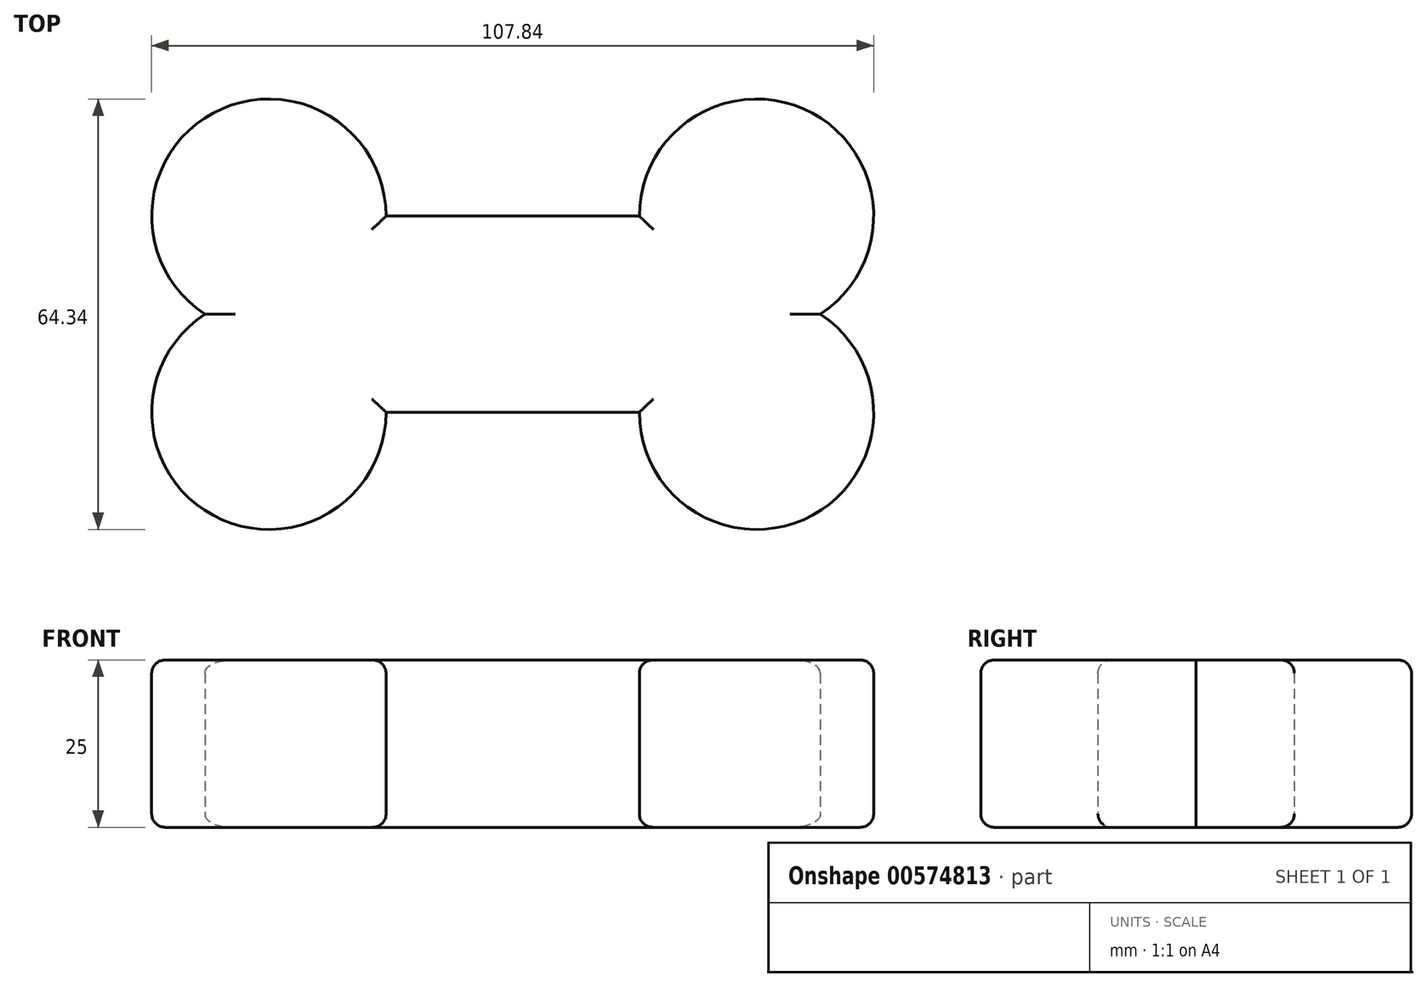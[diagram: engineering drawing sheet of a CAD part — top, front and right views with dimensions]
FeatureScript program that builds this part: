
annotation { "Feature Type Name" : "Feature", "Feature Type Description" : "" }
export const myFeature = defineFeature(function(context is Context, id is Id, definition is map)
    precondition{}
    {
        {
            var Q0;
            Q0=qCreatedBy(makeId("Top.planeOp"),FACE);
            var sketch = newSketch(context, id + "F0", { "sketchPlane" : qUnion([Q0])});
            skLineSegment(sketch, "E0.bottom", {"start": v(36.42, 14.67) * mm, "end": v(-36.42, 14.67) * mm});
            skLineSegment(sketch, "E0.top", {"start": v(36.42, -14.67) * mm, "end": v(-36.42, -14.67) * mm});
            skLineSegment(sketch, "E0.left", {"start": v(36.42, 14.67) * mm, "end": v(36.42, -14.67) * mm});
            skLineSegment(sketch, "E0.right", {"start": v(-36.42, 14.67) * mm, "end": v(-36.42, -14.67) * mm});
            skPoint(sketch, "E0.middle", {"position": v(0, 0) * mm});
            skCircle(sketch, "E1", {"center": v(36.42, 14.67) * mm, "radius": 17.5 * mm});
            skCircle(sketch, "E2", {"center": v(36.42, -14.67) * mm, "radius": 17.5 * mm});
            skCircle(sketch, "E3", {"center": v(-36.42, 14.67) * mm, "radius": 17.5 * mm});
            skCircle(sketch, "E4", {"center": v(-36.42, -14.67) * mm, "radius": 17.5 * mm});
            skSolve(sketch);
        }
        {
            var Q0;
            {var subQ0=sQuery(id+"F0.wireOp",EDGE,"E0.right");var subQ1=sQuery(id+"F0.wireOp",EDGE,"E0.top");var subQ2=makeQuery(id+"F0.imprint","INTERSECT",VERTEX,{"derivedFrom":[subQ1,subQ0]});Q0=makeQuery(id+"F0.imprint","IMPRINT",FACE,{"disambiguationData":[TD([[makeQuery(id+"F0.imprint","IMPRINT",EDGE,{"disambiguationData":[TD([[subQ2,1.0]])],"derivedFrom":subQ1}),1.0]])]});}
            var Q1;
            {var subQ0=sQuery(id+"F0.wireOp",EDGE,"E0.right");var subQ1=sQuery(id+"F0.wireOp",EDGE,"E0.top");var subQ2=makeQuery(id+"F0.imprint","INTERSECT",VERTEX,{"derivedFrom":[subQ1,subQ0]});Q1=makeQuery(id+"F0.imprint","IMPRINT",FACE,{"disambiguationData":[TD([[makeQuery(id+"F0.imprint","IMPRINT",EDGE,{"disambiguationData":[TD([[subQ2,1.0]])],"derivedFrom":subQ1}),-1.0]])]});}
            var Q2;
            {var subQ0=sQuery(id+"F0.wireOp",EDGE,"E0.left");var subQ1=sQuery(id+"F0.wireOp",EDGE,"E0.top");var subQ2=makeQuery(id+"F0.imprint","INTERSECT",VERTEX,{"derivedFrom":[subQ1,subQ0]});Q2=makeQuery(id+"F0.imprint","IMPRINT",FACE,{"disambiguationData":[TD([[makeQuery(id+"F0.imprint","IMPRINT",EDGE,{"disambiguationData":[TD([[subQ2,-1.0]])],"derivedFrom":subQ1}),1.0]])]});}
            var Q3;
            {var subQ0=sQuery(id+"F0.wireOp",EDGE,"E0.right");var subQ1=sQuery(id+"F0.wireOp",EDGE,"E0.bottom");var subQ2=makeQuery(id+"F0.imprint","INTERSECT",VERTEX,{"derivedFrom":[subQ1,subQ0]});Q3=makeQuery(id+"F0.imprint","IMPRINT",FACE,{"disambiguationData":[TD([[makeQuery(id+"F0.imprint","IMPRINT",EDGE,{"disambiguationData":[TD([[subQ2,1.0]])],"derivedFrom":subQ1}),-1.0]])]});}
            var Q4;
            {var subQ0=sQuery(id+"F0.wireOp",EDGE,"E4");var subQ1=sQuery(id+"F0.wireOp",EDGE,"E0.right");var subQ2=makeQuery(id+"F0.imprint","INTERSECT",VERTEX,{"derivedFrom":[subQ1,subQ0]});Q4=makeQuery(id+"F0.imprint","IMPRINT",FACE,{"disambiguationData":[TD([[makeQuery(id+"F0.imprint","IMPRINT",EDGE,{"disambiguationData":[TD([[subQ2,-1.0]])],"derivedFrom":subQ1}),-1.0]])]});}
            var Q5;
            {var subQ0=sQuery(id+"F0.wireOp",EDGE,"E4");var subQ1=sQuery(id+"F0.wireOp",EDGE,"E0.right");var subQ2=makeQuery(id+"F0.imprint","INTERSECT",VERTEX,{"derivedFrom":[subQ1,subQ0]});Q5=makeQuery(id+"F0.imprint","IMPRINT",FACE,{"disambiguationData":[TD([[makeQuery(id+"F0.imprint","IMPRINT",EDGE,{"disambiguationData":[TD([[subQ2,-1.0]])],"derivedFrom":subQ1}),1.0]])]});}
            var Q6;
            {var subQ0=sQuery(id+"F0.wireOp",EDGE,"E0.left");var subQ1=sQuery(id+"F0.wireOp",EDGE,"E0.bottom");var subQ2=makeQuery(id+"F0.imprint","INTERSECT",VERTEX,{"derivedFrom":[subQ1,subQ0]});Q6=makeQuery(id+"F0.imprint","IMPRINT",FACE,{"disambiguationData":[TD([[makeQuery(id+"F0.imprint","IMPRINT",EDGE,{"disambiguationData":[TD([[subQ2,-1.0]])],"derivedFrom":subQ1}),-1.0]])]});}
            var Q7;
            {var subQ0=sQuery(id+"F0.wireOp",EDGE,"E0.left");var subQ1=sQuery(id+"F0.wireOp",EDGE,"E0.top");var subQ2=makeQuery(id+"F0.imprint","INTERSECT",VERTEX,{"derivedFrom":[subQ1,subQ0]});Q7=makeQuery(id+"F0.imprint","IMPRINT",FACE,{"disambiguationData":[TD([[makeQuery(id+"F0.imprint","IMPRINT",EDGE,{"disambiguationData":[TD([[subQ2,-1.0]])],"derivedFrom":subQ1}),-1.0]])]});}
            var Q8;
            {var subQ3=sQuery(id+"F0.wireOp",EDGE,"E1");var subQ5=sQuery(id+"F0.wireOp",EDGE,"E0.bottom");var subQ6=makeQuery(id+"F0.imprint","INTERSECT",VERTEX,{"derivedFrom":[subQ5,subQ3]});Q8=makeQuery(id+"F0.imprint","IMPRINT",FACE,{"disambiguationData":[TD([[makeQuery(id+"F0.imprint","IMPRINT",EDGE,{"disambiguationData":[TD([[subQ6,-1.0]])],"derivedFrom":subQ5}),1.0]])]});}
            var Q9;
            {var subQ0=sQuery(id+"F0.wireOp",EDGE,"E0.right");var subQ1=sQuery(id+"F0.wireOp",EDGE,"E0.bottom");var subQ2=makeQuery(id+"F0.imprint","INTERSECT",VERTEX,{"derivedFrom":[subQ1,subQ0]});Q9=makeQuery(id+"F0.imprint","IMPRINT",FACE,{"disambiguationData":[TD([[makeQuery(id+"F0.imprint","IMPRINT",EDGE,{"disambiguationData":[TD([[subQ2,1.0]])],"derivedFrom":subQ1}),1.0]])]});}
            var Q10;
            {var subQ0=sQuery(id+"F0.wireOp",EDGE,"E0.left");var subQ1=sQuery(id+"F0.wireOp",EDGE,"E0.bottom");var subQ2=makeQuery(id+"F0.imprint","INTERSECT",VERTEX,{"derivedFrom":[subQ1,subQ0]});Q10=makeQuery(id+"F0.imprint","IMPRINT",FACE,{"disambiguationData":[TD([[makeQuery(id+"F0.imprint","IMPRINT",EDGE,{"disambiguationData":[TD([[subQ2,-1.0]])],"derivedFrom":subQ1}),1.0]])]});}
            var Q11;
            {var subQ0=sQuery(id+"F0.wireOp",EDGE,"E2");var subQ1=sQuery(id+"F0.wireOp",EDGE,"E0.left");var subQ2=makeQuery(id+"F0.imprint","INTERSECT",VERTEX,{"derivedFrom":[subQ1,subQ0]});Q11=makeQuery(id+"F0.imprint","IMPRINT",FACE,{"disambiguationData":[TD([[makeQuery(id+"F0.imprint","IMPRINT",EDGE,{"disambiguationData":[TD([[subQ2,-1.0]])],"derivedFrom":subQ1}),1.0]])]});}
            var Q12;
            {var subQ0=sQuery(id+"F0.wireOp",EDGE,"E2");var subQ1=sQuery(id+"F0.wireOp",EDGE,"E0.left");var subQ2=makeQuery(id+"F0.imprint","INTERSECT",VERTEX,{"derivedFrom":[subQ1,subQ0]});Q12=makeQuery(id+"F0.imprint","IMPRINT",FACE,{"disambiguationData":[TD([[makeQuery(id+"F0.imprint","IMPRINT",EDGE,{"disambiguationData":[TD([[subQ2,-1.0]])],"derivedFrom":subQ1}),-1.0]])]});}
            extrude(context, id + "F1", {"entities" : qUnion([Q0, Q1, Q2, Q3, Q4, Q5, Q6, Q7, Q8, Q9, Q10, Q11, Q12]), "depth" : 25 * mm, "offsetDistance" : 25 * mm});
        }
        {
            var Q0;
            Q0=makeQuery(id+"F1.opExtrude","CAP_EDGE",EDGE,{"disambiguationData":[OSD([sQuery(id+"F0.wireOp",EDGE,"E4")])],"isStart":false});
            var Q1;
            Q1=makeQuery(id+"F1.opExtrude","CAP_EDGE",EDGE,{"disambiguationData":[OSD([sQuery(id+"F0.wireOp",EDGE,"E4")])],"isStart":true});
            var Q2;
            Q2=makeQuery(id+"F1.opExtrude","CAP_EDGE",EDGE,{"disambiguationData":[OSD([sQuery(id+"F0.wireOp",EDGE,"E3")])],"isStart":true});
            var Q3;
            Q3=makeQuery(id+"F1.opExtrude","CAP_EDGE",EDGE,{"disambiguationData":[OSD([sQuery(id+"F0.wireOp",EDGE,"E3")])],"isStart":false});
            var Q4;
            Q4=makeQuery(id+"F1.opExtrude","CAP_EDGE",EDGE,{"disambiguationData":[OSD([sQuery(id+"F0.wireOp",EDGE,"E1")])],"isStart":false});
            var Q5;
            Q5=makeQuery(id+"F1.opExtrude","CAP_EDGE",EDGE,{"disambiguationData":[OSD([sQuery(id+"F0.wireOp",EDGE,"E1")])],"isStart":true});
            var Q6;
            Q6=makeQuery(id+"F1.opExtrude","CAP_EDGE",EDGE,{"disambiguationData":[OSD([sQuery(id+"F0.wireOp",EDGE,"E2")])],"isStart":false});
            var Q7;
            Q7=makeQuery(id+"F1.opExtrude","CAP_EDGE",EDGE,{"disambiguationData":[OSD([sQuery(id+"F0.wireOp",EDGE,"E2")])],"isStart":true});
            fillet(context, id + "F2", {"entities" : qUnion([Q0, Q1, Q2, Q3, Q4, Q5, Q6, Q7]), "radius" : 2 * mm, "tangentPropagation" : true, "allowEdgeOverflow" : false});
        }
        {
            var Q0;
            Q0=makeQuery(id+"F1.opExtrude","CAP_EDGE",EDGE,{"disambiguationData":[OSD([sQuery(id+"F0.wireOp",EDGE,"E0.bottom")])],"isStart":false});
            var Q1;
            Q1=makeQuery(id+"F1.opExtrude","CAP_EDGE",EDGE,{"disambiguationData":[OSD([sQuery(id+"F0.wireOp",EDGE,"E0.top")])],"isStart":false});
            var Q2;
            Q2=makeQuery(id+"F1.opExtrude","CAP_EDGE",EDGE,{"disambiguationData":[OSD([sQuery(id+"F0.wireOp",EDGE,"E0.bottom")])],"isStart":true});
            var Q3;
            Q3=makeQuery(id+"F1.opExtrude","CAP_EDGE",EDGE,{"disambiguationData":[OSD([sQuery(id+"F0.wireOp",EDGE,"E0.top")])],"isStart":true});
            fillet(context, id + "F3", {"entities" : qUnion([Q0, Q1, Q2, Q3]), "radius" : 2 * mm, "tangentPropagation" : true, "allowEdgeOverflow" : false});
        }
    });
